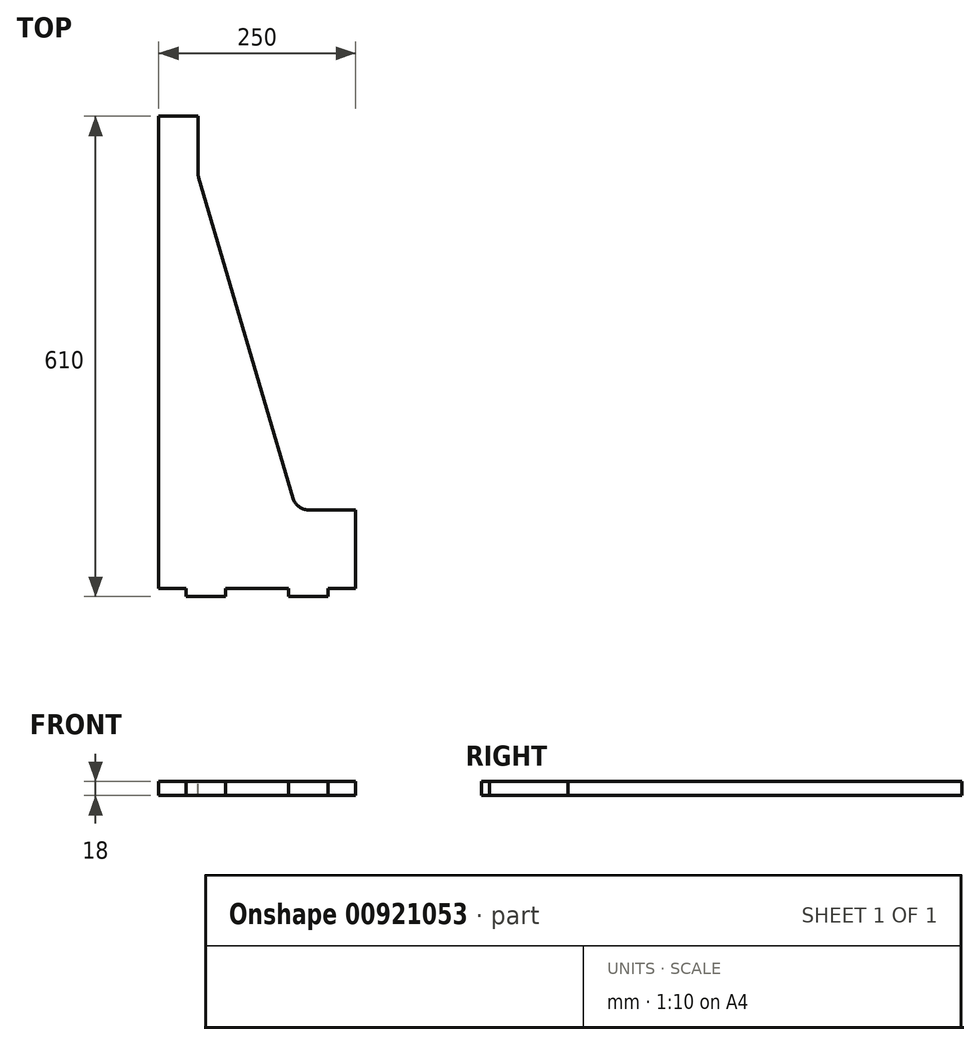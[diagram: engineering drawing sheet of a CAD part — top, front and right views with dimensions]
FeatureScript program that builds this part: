
annotation { "Feature Type Name" : "Feature", "Feature Type Description" : "" }
export const myFeature = defineFeature(function(context is Context, id is Id, definition is map)
    precondition{}
    {
        {
            var Q0;
            Q0=qCreatedBy(makeId("Top.planeOp"),FACE);
            var sketch = newSketch(context, id + "F0", { "sketchPlane" : qUnion([Q0])});
            skLineSegment(sketch, "E0.bottom", {"start": v(-91.83, 528.33) * mm, "end": v(158.17, 528.33) * mm});
            skLineSegment(sketch, "E0.top", {"start": v(-91.83, -71.67) * mm, "end": v(-56.83, -71.67) * mm});
            skLineSegment(sketch, "E0.left", {"start": v(-91.83, 528.33) * mm, "end": v(-91.83, -71.67) * mm});
            skLineSegment(sketch, "E0.right", {"start": v(158.17, 528.33) * mm, "end": v(158.17, -71.67) * mm});
            skLineSegment(sketch, "E1.top", {"start": v(123.17, -81.67) * mm, "end": v(73.17, -81.67) * mm});
            skLineSegment(sketch, "E1.left", {"start": v(123.17, -71.67) * mm, "end": v(123.17, -81.67) * mm});
            skLineSegment(sketch, "E1.right", {"start": v(73.17, -71.67) * mm, "end": v(73.17, -81.67) * mm});
            skLineSegment(sketch, "E2.top", {"start": v(-56.83, -81.67) * mm, "end": v(-6.83, -81.67) * mm});
            skLineSegment(sketch, "E2.left", {"start": v(-56.83, -71.67) * mm, "end": v(-56.83, -81.67) * mm});
            skLineSegment(sketch, "E2.right", {"start": v(-6.83, -71.67) * mm, "end": v(-6.83, -81.67) * mm});
            skLineSegment(sketch, "E3.trimOffspring", {"start": v(-6.83, -71.67) * mm, "end": v(73.17, -71.67) * mm});
            skLineSegment(sketch, "E4.trimOffspring", {"start": v(123.17, -71.67) * mm, "end": v(158.17, -71.67) * mm});
            skSolve(sketch);
        }
        {
            var Q0;
            Q0=makeQuery(id+"F0.imprint","IMPRINT",FACE,{"disambiguationData":[TD([[makeQuery(id+"F0.imprint","IMPRINT",EDGE,{"derivedFrom":sQuery(id+"F0.wireOp",EDGE,"E0.bottom")}),-1.0]])]});
            extrude(context, id + "F1", {"entities" : qUnion([Q0]), "depth" : 18 * mm, "offsetDistance" : 25 * mm});
        }
        {
            var Q0;
            Q0=makeQuery(id+"F1.opExtrude","CAP_FACE",FACE,{"disambiguationData":[OSD([sQuery(id+"F0.wireOp",EDGE,"E0.bottom"),sQuery(id+"F0.wireOp",EDGE,"E0.top"),sQuery(id+"F0.wireOp",EDGE,"E0.left"),sQuery(id+"F0.wireOp",EDGE,"E0.right")])],"isStart":false});
            var sketch = newSketch(context, id + "F2", { "sketchPlane" : qUnion([Q0])});
            skLineSegment(sketch, "E5", {"start": v(-91.83, 528.33) * mm, "end": v(-41.83, 528.33) * mm});
            skLineSegment(sketch, "E6", {"start": v(-41.83, 528.33) * mm, "end": v(-41.83, 453.33) * mm});
            skLineSegment(sketch, "E7", {"start": v(158.17, -71.67) * mm, "end": v(158.17, 28.33) * mm});
            skLineSegment(sketch, "E8", {"start": v(158.17, 28.33) * mm, "end": v(83.17, 28.33) * mm});
            skLineSegment(sketch, "E9", {"start": v(83.17, 28.33) * mm, "end": v(-41.83, 453.33) * mm});
            skSolve(sketch);
        }
        {
            var Q0;
            {var subQ3=sQuery(id+"F2.wireOp",EDGE,"E6");Q0=makeQuery(id+"F2.imprint","IMPRINT",FACE,{"disambiguationData":[TD([[makeQuery(id+"F2.imprint","IMPRINT",EDGE,{"derivedFrom":subQ3}),1.0]])]});}
            extrude(context, id + "F3", {"entities" : qUnion([Q0]), "operationType" : NewBodyOperationType.REMOVE, "oppositeDirection" : true, "depth" : 25 * mm, "offsetDistance" : 25 * mm});
        }
        {
            var Q0;
            Q0=makeQuery(id+"F3.boolean.opBoolean","COPY",EDGE,{"derivedFrom":makeQuery(id+"F3.opExtrude","SWEPT_EDGE",EDGE,{"disambiguationData":[OSD([sQuery(id+"F0.wireOp",EDGE,"E0.bottom"),sQuery(id+"F2.wireOp",EDGE,"E5"),sQuery(id+"F2.wireOp",EDGE,"E6")])]})});
            var Q1;
            Q1=makeQuery(id+"F3.boolean.opBoolean","COPY",EDGE,{"derivedFrom":makeQuery(id+"F3.opExtrude","SWEPT_EDGE",EDGE,{"disambiguationData":[OSD([sQuery(id+"F0.wireOp",EDGE,"E0.right"),sQuery(id+"F2.wireOp",EDGE,"E7"),sQuery(id+"F2.wireOp",EDGE,"E8")])]})});
            var Q2;
            Q2=makeQuery(id+"F3.boolean.opBoolean","COPY",EDGE,{"derivedFrom":makeQuery(id+"F3.opExtrude","SWEPT_EDGE",EDGE,{"disambiguationData":[OSD([sQuery(id+"F2.wireOp",EDGE,"E6"),sQuery(id+"F2.wireOp",EDGE,"E9")])]})});
            var Q3;
            Q3=makeQuery(id+"F3.boolean.opBoolean","COPY",EDGE,{"derivedFrom":makeQuery(id+"F3.opExtrude","SWEPT_EDGE",EDGE,{"disambiguationData":[OSD([sQuery(id+"F2.wireOp",EDGE,"E8"),sQuery(id+"F2.wireOp",EDGE,"E9")])]})});
            fillet(context, id + "F4", {"entities" : qUnion([Q0, Q1, Q2, Q3]), "radius" : 20 * mm, "tangentPropagation" : true, "allowEdgeOverflow" : false});
        }
    });
